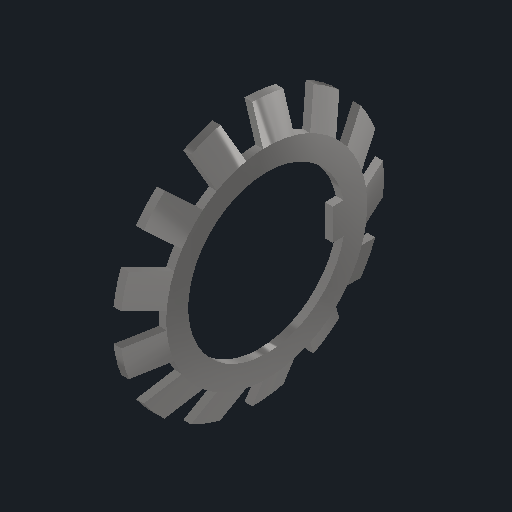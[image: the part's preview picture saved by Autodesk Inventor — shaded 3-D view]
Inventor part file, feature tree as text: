
AUTODESK INVENTOR PART (.ipt)
format: ipt  version: 2022 (Build 260153000, 153)  size: 223,744 bytes
history: native  units: mm (DEFAULTED — no unit token found)
features: other x21, sketch x3, extrude x2, revolve x1
ambient origin geometry x8: Origin, YZ Plane, XZ Plane, XY Plane, X Axis, Y Axis, Z Axis, Center Point
bodies: Solid1 (feature_tree)
feature tree (27):
  revolve  "Revolution1"  [1 undecoded]
  extrude  "Extrusion1"  TaperAngle=0.0deg  [1 undecoded]
  extrude  "Extrusion2"  [1 undecoded]
  other  "mb_XY"
  other  "mb_YZ"
  other  "mb_ZX"
  other  "mb_X"
  other  "mb_Y"
  other  "mb_Z"
  other  "mb_Center"
  other  "mb2_XY"
  other  "mb2_YZ"
  other  "mb2_ZX"
  other  "mb2_X"
  other  "mb2_Y"
  other  "mb2_Z"
  other  "mb2_Center"
  other  "to_locknut_XY"
  other  "to_locknut_YZ"
  other  "to_locknut_ZX"
  other  "to_locknut_X"
  other  "to_locknut_Y"
  other  "to_locknut_Z"
  other  "to_locknut_Center"
  sketch  "Sketch_1"  dims[d0=360.0deg d1=25.0mm d2=0.0mm]
  sketch  "Sketch_2"  dims[d3=1.25mm d4=0.0mm d5=0.0mm]
  sketch  "Sketch_7"
note: 3 required parameter values undecoded (feature->parameter linkage not recoverable at this tier; creation-order binding heuristic only, values carry confidence <= 0.55)